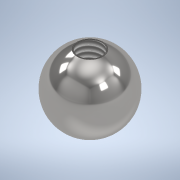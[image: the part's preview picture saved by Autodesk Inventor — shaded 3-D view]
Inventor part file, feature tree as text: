
AUTODESK INVENTOR PART (.ipt)
format: ipt  version: 2022 (Build 260153000, 153)  size: 142,336 bytes
history: native  units: mm
features: sketch x2, revolve x1, hole x1, plane x1
ambient origin geometry x8: Origin, YZ Plane, XZ Plane, XY Plane, X Axis, Y Axis, Z Axis, Center Point
bodies: Solid1 (feature_tree)
feature tree (5):
  revolve  "Revolution1"  Angle=90.0deg
  hole  "Hole1"  [1 undecoded]
  plane  "Work Plane1"
  sketch  "Sketch1"  dims[d0=10.0mm d2=90.0deg]
  sketch  "Sketch2"  dims[d3=3.242mm d4=5.0mm d5=6.0mm d6=2.0mm d7=90.0deg d8=5.0mm d9=0.0mm d10=3.5mm d11=0.0mm]
note: 1 required parameter value undecoded (feature->parameter linkage not recoverable at this tier; creation-order binding heuristic only, values carry confidence <= 0.55)
